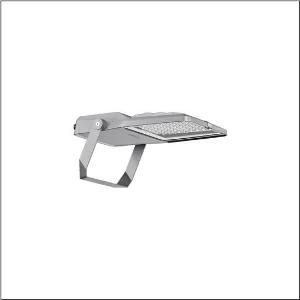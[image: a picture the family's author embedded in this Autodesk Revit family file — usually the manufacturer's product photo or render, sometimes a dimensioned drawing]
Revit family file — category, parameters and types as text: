
# Revit family: floodlight_fl_21_iq_mini___pl52_5xa7772b5d1a_4874
name_source: partatom
category: Lighting Fixtures
units: mm (PartAtom-declared; Revit-internal decimal feet)

## family parameters
Cut with Voids When Loaded = No
Host = Face
Light Source = No
Part Type = Normal
Room Calculation Point = No
Round Connector Dimension = Use Diameter
Shared = No

## types (1)
- --- (1 x LED, 5820 lm, 45.5 W, 4000K)
    Apparent Load = 46 VA
    CIE Flux Codes = 26 60 98 100 100
    Color Rendering = 80
    Color Temperature = 4000K
    Default Elevation = 1800 mm
    Description = Floodlight FL 21 iQ mini, floodlight, primary light control with lens, of PMMA, primary optical cover: protective disc, of toughened safety glass, transparent, light distribution: PL52, light emission: direct distribution, installation type: surface-mounted, lamps: LED, High Power LED, rated values: 5.820lm | 45,5W | 127,9lm/W (begin service life); end service life: 5.820lm | 48W; at 50% lumin. flux: 2.910lm | 21,5W | 135,3lm/W, colour temperature: 4000K, colour rendering: CRI > 80, light colour: 840, light setting 1 begin service life: 100% | 5.820lm | 45,5W | 127,9lm/W | 4.000K, light setting 1 end service life: 48W, further light settings possible, control: Street-Remote, Auto-Match, Temp-Guard, Night-Set, Smart-Wire, Desk-Remote (wireless, voltage-free reading and setting of iQ features in the workshop via application-optimized NFC function/RFID function), optimised constant luminous flux control (CLO 2.0), pre-setting: linear dimming characteristic, with terminal, 6-pole, mains connection: 220..240V, AC, 50/60Hz, luminaire housing, of diecast aluminium, powder-coated, SITECO metallic grey (DB 702S), corrosivity category C5 mid according to DIN EN ISO 12944suitable for swimming poolschlorine-resistant, sealing non-destructively replaceable, mounting bracket, of steel, galvanised, powder-coated, SITECO metallic grey (DB 702S), protection rating (complete): IP66, insulation class (complete): insulation class II (safety insulation), certification: CE, ENEC, VDE, protection symbol: D, impact resistance: IK08, permissible operating ambient temperature: -40..+40°C, permissible operating ambient temperature for outdoor applications: -40..+50°C, standard: DIN EN 12944, LABS conformity tested according to VDMA 24364:2018-05, packaging unit: 1 piece

Light Distribution: PL52
    Height = 70 mm
    Lamp = 1 x LED
    Lamp Light Flux = 5820 lm
    Lamp Power = 45.5 W
    Lamp count = 1
    Length = 485 mm
    Luminous efficacy = 128 lm/W
    Manufacturer = Siteco
    ModVariant = No
    Model = 5XA7772B5D1A
    Mounting Place = Pole
    Mounting Type = Pole annexe
    Number of Poles = 1
    OnlyDefault = Yes
    Power Factor = 1
    Product Name = Floodlight FL 21 iQ mini | PL52
    Product group = floodlight | pylon annexe
    ProductGroupID = 6201
    Protection Class = Protection class II
    Protection Degree = IP 66
    RLX_Detail_Level = 1
    RLX_Emergency_Light_Flux = 0 lm
    RLX_Emergency_Type = 0
    RLX_Emergency_Type_DB = No
    RlxData = <blob elided: 96621 chars, md5=d5cb9d60>
    Socket = socket
    Standby Power = 0 W
    System Light Flux = 5820 lm
    System Power = 46 W
    Type Comments = factory setting: luminous flux: 100 % | dim-lin: 254 | 463 mA
    Type Image = l_1006845.jpg
    URL = http://relux.com
    VarID = @adj_165689
    Voltage = 0 V
    Weight = 0.00 kg
    Width = 337 mm

## geometry (parser evidence)
native form markers: Blend x4, Sweep x12
no freeform markers — native parametric forms only
